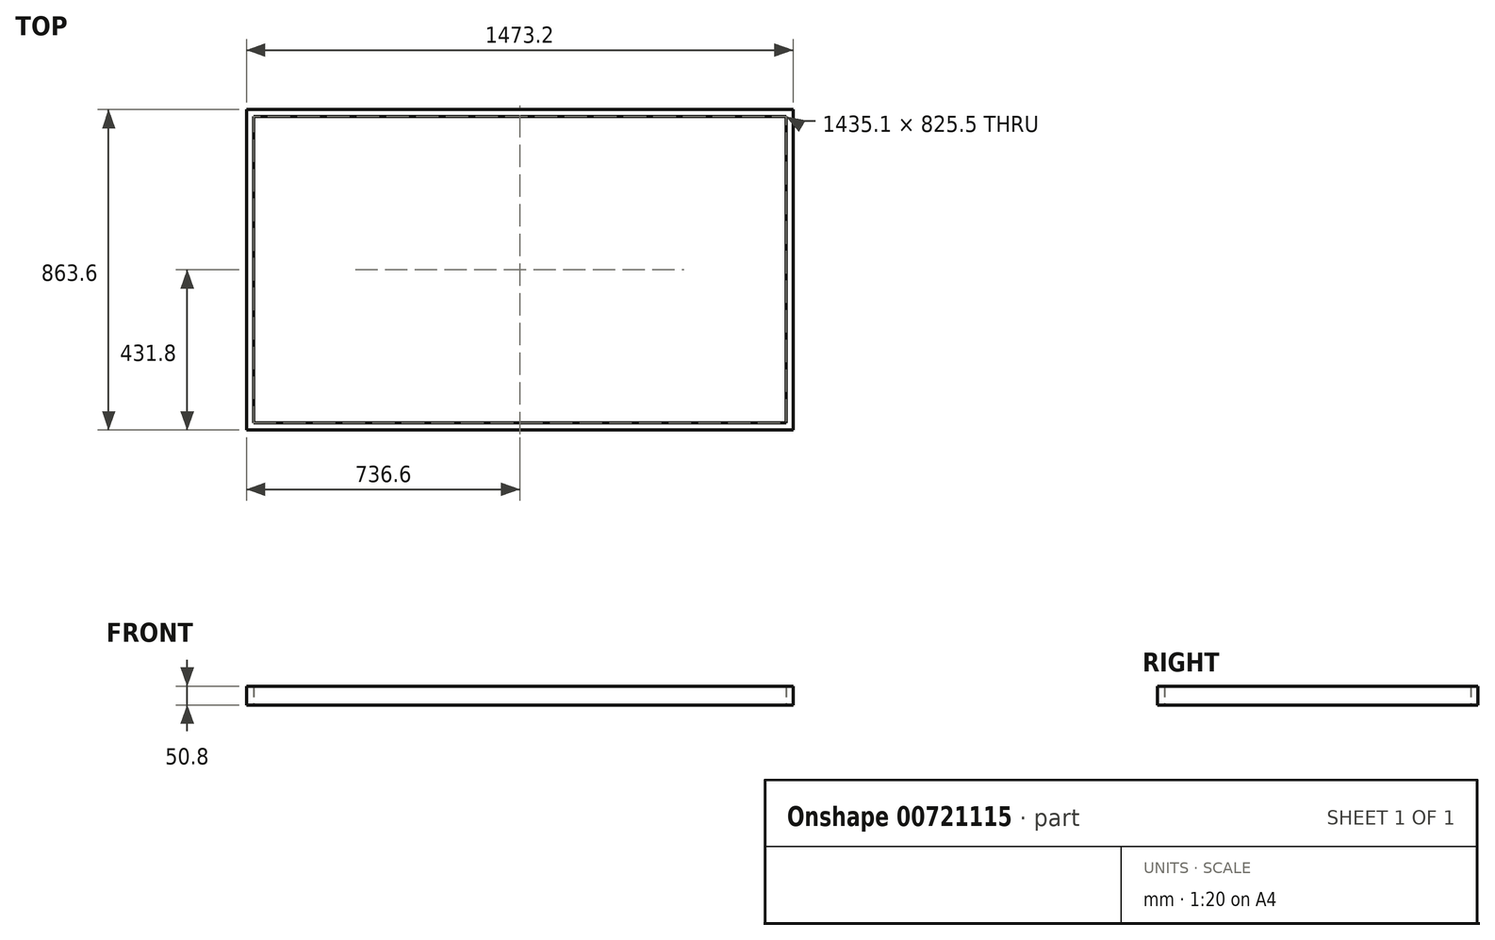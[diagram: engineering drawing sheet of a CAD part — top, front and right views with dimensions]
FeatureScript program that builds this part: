
annotation { "Feature Type Name" : "Feature", "Feature Type Description" : "" }
export const myFeature = defineFeature(function(context is Context, id is Id, definition is map)
    precondition{}
    {
        {
            var Q0;
            Q0=qCreatedBy(makeId("Top.planeOp"),FACE);
            var sketch = newSketch(context, id + "F0", { "sketchPlane" : qUnion([Q0])});
            skLineSegment(sketch, "E0.bottom", {"start": v(736.6, 431.8) * mm, "end": v(-736.6, 431.8) * mm});
            skLineSegment(sketch, "E0.top", {"start": v(736.6, -431.8) * mm, "end": v(-736.6, -431.8) * mm});
            skLineSegment(sketch, "E0.left", {"start": v(736.6, 431.8) * mm, "end": v(736.6, -431.8) * mm});
            skLineSegment(sketch, "E0.right", {"start": v(-736.6, 431.8) * mm, "end": v(-736.6, -431.8) * mm});
            skPoint(sketch, "E0.middle", {"position": v(0, 0) * mm});
            skLineSegment(sketch, "E1.bottom", {"start": v(-717.55, 412.75) * mm, "end": v(717.55, 412.75) * mm});
            skLineSegment(sketch, "E1.top", {"start": v(-717.55, -412.75) * mm, "end": v(717.55, -412.75) * mm});
            skLineSegment(sketch, "E1.left", {"start": v(-717.55, 412.75) * mm, "end": v(-717.55, -412.75) * mm});
            skLineSegment(sketch, "E1.right", {"start": v(717.55, 412.75) * mm, "end": v(717.55, -412.75) * mm});
            skSolve(sketch);
        }
        {
            var Q0;
            Q0=makeQuery(id+"F0.imprint","IMPRINT",FACE,{"disambiguationData":[TD([[makeQuery(id+"F0.imprint","IMPRINT",EDGE,{"derivedFrom":sQuery(id+"F0.wireOp",EDGE,"E0.bottom")}),1.0]])]});
            extrude(context, id + "F1", {"entities" : qUnion([Q0]), "depth" : 50.8 * mm, "offsetDistance" : 25.4 * mm});
        }
    });
